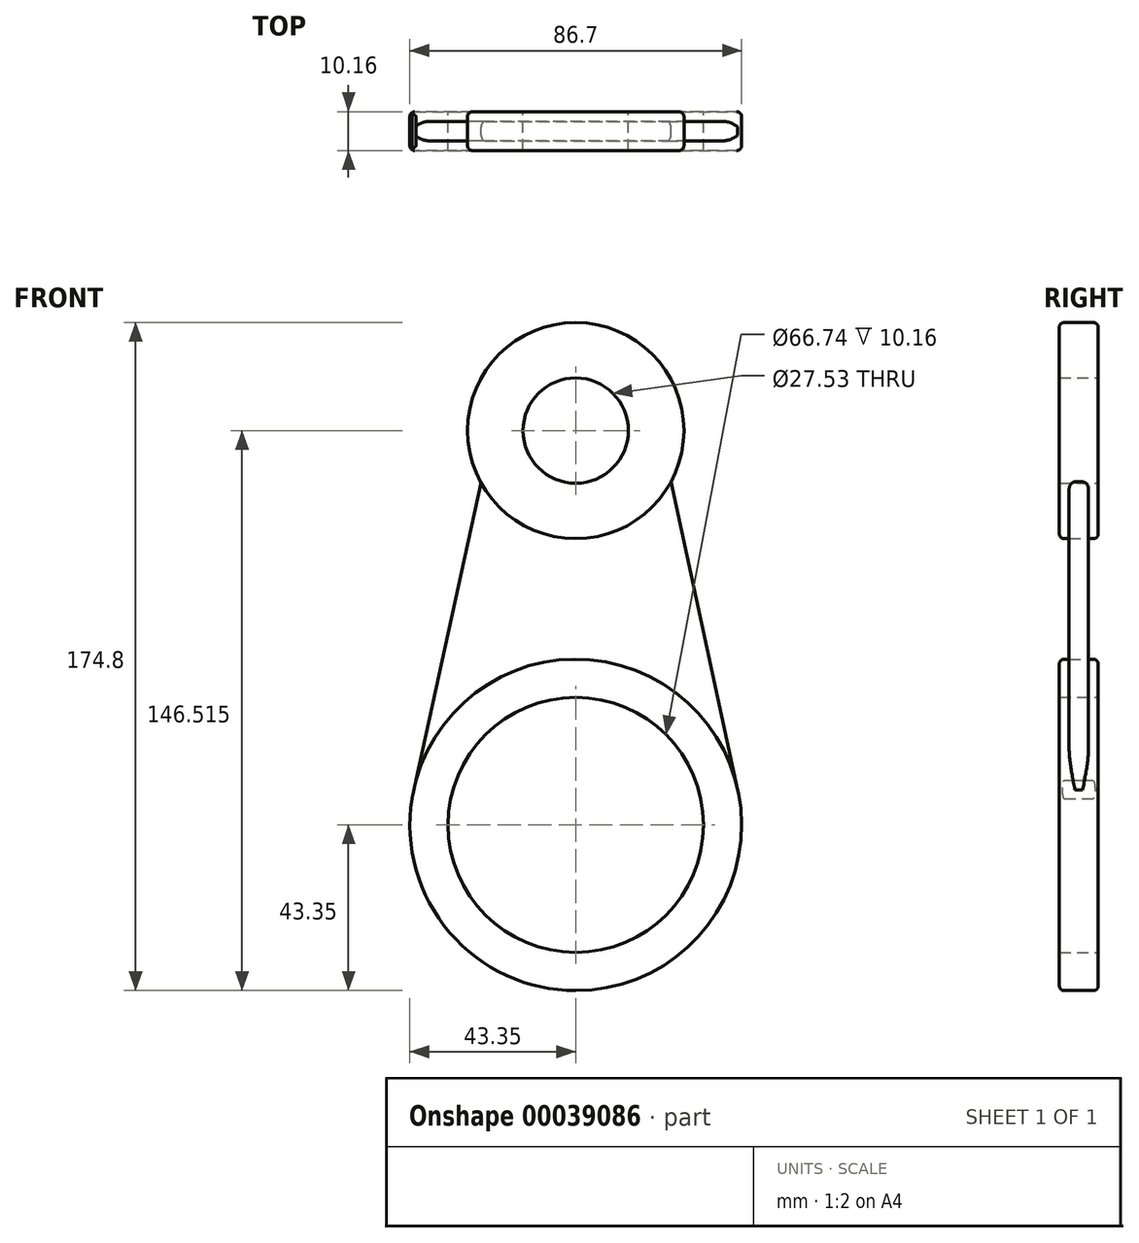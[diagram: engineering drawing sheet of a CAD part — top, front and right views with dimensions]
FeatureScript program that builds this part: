
annotation { "Feature Type Name" : "Feature", "Feature Type Description" : "" }
export const myFeature = defineFeature(function(context is Context, id is Id, definition is map)
    precondition{}
    {
        {
            var Q0;
            Q0=qCreatedBy(makeId("Front.planeOp"),FACE);
            var sketch = newSketch(context, id + "F0", { "sketchPlane" : qUnion([Q0])});
            skCircle(sketch, "E0", {"center": v(0, 0) * mm, "radius": 43.35 * mm});
            skCircle(sketch, "E1", {"center": v(0, 0) * mm, "radius": 33.37 * mm});
            skCircle(sketch, "E2", {"center": v(0, 103.17) * mm, "radius": 13.77 * mm});
            skCircle(sketch, "E3", {"center": v(0, 103.17) * mm, "radius": 28.28 * mm});
            skLineSegment(sketch, "E4", {"start": v(-24.76, 89.5) * mm, "end": v(-42.81, 6.82) * mm});
            skLineSegment(sketch, "E5", {"start": v(24.9, 89.76) * mm, "end": v(42.37, 9.18) * mm});
            skSolve(sketch);
        }
        {
            var Q0;
            Q0=makeQuery(id+"F0.imprint","IMPRINT",FACE,{"disambiguationData":[TD([[makeQuery(id+"F0.imprint","IMPRINT",EDGE,{"derivedFrom":sQuery(id+"F0.wireOp",EDGE,"E2")}),-1.0]])]});
            var Q1;
            Q1=makeQuery(id+"F0.imprint","IMPRINT",FACE,{"disambiguationData":[TD([[makeQuery(id+"F0.imprint","IMPRINT",EDGE,{"derivedFrom":sQuery(id+"F0.wireOp",EDGE,"E1")}),-1.0]])]});
            extrude(context, id + "F1", {"entities" : qUnion([Q0, Q1]), "depth" : 5.08 * mm, "hasSecondDirection" : true, "secondDirectionOppositeDirection" : true, "secondDirectionDepth" : 5.08 * mm});
        }
        {
            var Q0;
            {var subQ0=sQuery(id+"F0.wireOp",EDGE,"E5");Q0=makeQuery(id+"F0.imprint","IMPRINT",FACE,{"disambiguationData":[TD([[makeQuery(id+"F0.imprint","IMPRINT",EDGE,{"derivedFrom":subQ0}),-1.0]])]});}
            extrude(context, id + "F2", {"entities" : qUnion([Q0]), "depth" : 2.54 * mm, "hasSecondDirection" : true, "secondDirectionOppositeDirection" : true, "secondDirectionDepth" : 2.54 * mm});
        }
        {
            var Q0;
            Q0=makeQuery(id+"F1.opExtrude","CAP_EDGE",EDGE,{"disambiguationData":[OSD([sQuery(id+"F0.wireOp",EDGE,"E3")])],"isStart":false});
            var Q1;
            Q1=makeQuery(id+"F1.opExtrude","CAP_EDGE",EDGE,{"disambiguationData":[OSD([sQuery(id+"F0.wireOp",EDGE,"E0")])],"isStart":false});
            var Q2;
            Q2=makeQuery(id+"F1.opExtrude","CAP_EDGE",EDGE,{"disambiguationData":[OSD([sQuery(id+"F0.wireOp",EDGE,"E3")])],"isStart":true});
            var Q3;
            Q3=makeQuery(id+"F1.opExtrude","CAP_EDGE",EDGE,{"disambiguationData":[OSD([sQuery(id+"F0.wireOp",EDGE,"E0")])],"isStart":true});
            fillet(context, id + "F3", {"entities" : qUnion([Q0, Q1, Q2, Q3]), "radius" : 1.27 * mm, "tangentPropagation" : true, "allowEdgeOverflow" : false});
        }
        {
            var Q0;
            Q0=makeQuery(id+"F2.opExtrude","CAP_EDGE",EDGE,{"disambiguationData":[OSD([sQuery(id+"F0.wireOp",EDGE,"E4")])],"isStart":false});
            var Q1;
            Q1=makeQuery(id+"F2.opExtrude","CAP_EDGE",EDGE,{"disambiguationData":[OSD([sQuery(id+"F0.wireOp",EDGE,"E4")])],"isStart":true});
            var Q2;
            Q2=makeQuery(id+"F2.opExtrude","CAP_EDGE",EDGE,{"disambiguationData":[OSD([sQuery(id+"F0.wireOp",EDGE,"E5")])],"isStart":false});
            var Q3;
            Q3=makeQuery(id+"F2.opExtrude","CAP_EDGE",EDGE,{"disambiguationData":[OSD([sQuery(id+"F0.wireOp",EDGE,"E5")])],"isStart":true});
            fillet(context, id + "F4", {"entities" : qUnion([Q0, Q1, Q2, Q3]), "radius" : 1.52 * mm, "tangentPropagation" : true, "allowEdgeOverflow" : false});
        }
    });
